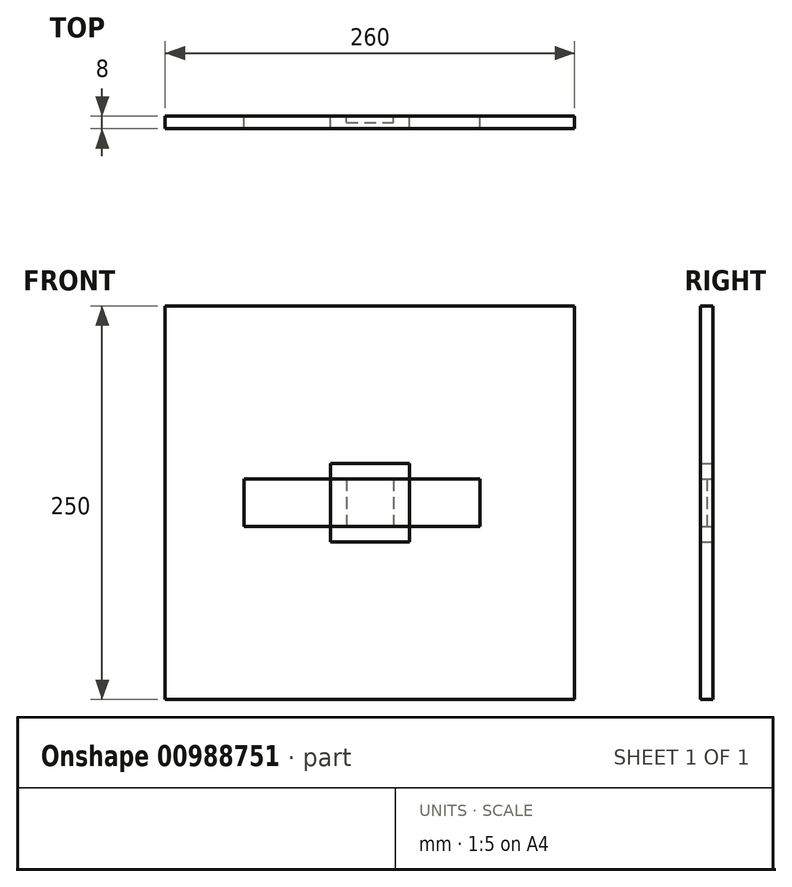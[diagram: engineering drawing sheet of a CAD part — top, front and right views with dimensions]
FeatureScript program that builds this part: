
annotation { "Feature Type Name" : "Feature", "Feature Type Description" : "" }
export const myFeature = defineFeature(function(context is Context, id is Id, definition is map)
    precondition{}
    {
        {
            var Q0;
            Q0=qCreatedBy(makeId("Front.planeOp"),FACE);
            var sketch = newSketch(context, id + "F0", { "sketchPlane" : qUnion([Q0])});
            skLineSegment(sketch, "E0.bottom", {"start": v(-130, 125) * mm, "end": v(130, 125) * mm});
            skLineSegment(sketch, "E0.top", {"start": v(-130, -125) * mm, "end": v(130, -125) * mm});
            skLineSegment(sketch, "E0.left", {"start": v(-130, 125) * mm, "end": v(-130, -125) * mm});
            skLineSegment(sketch, "E0.right", {"start": v(130, 125) * mm, "end": v(130, -125) * mm});
            skSolve(sketch);
        }
        {
            var Q0;
            Q0=makeQuery(id+"F0.imprint","IMPRINT",FACE,{"disambiguationData":[TD([[makeQuery(id+"F0.imprint","IMPRINT",EDGE,{"derivedFrom":sQuery(id+"F0.wireOp",EDGE,"E0.bottom")}),-1.0]])]});
            extrude(context, id + "F1", {"entities" : qUnion([Q0]), "depth" : 8 * mm, "offsetDistance" : 25 * mm});
        }
        {
            var Q0;
            Q0=qCreatedBy(makeId("Front.planeOp"),FACE);
            var sketch = newSketch(context, id + "F2", { "sketchPlane" : qUnion([Q0])});
            skLineSegment(sketch, "E1.bottom", {"start": v(-15, 15) * mm, "end": v(15, 15) * mm});
            skLineSegment(sketch, "E1.top", {"start": v(-15, -15) * mm, "end": v(15, -15) * mm});
            skLineSegment(sketch, "E1.left", {"start": v(-15, 15) * mm, "end": v(-15, -15) * mm});
            skLineSegment(sketch, "E1.right", {"start": v(15, 15) * mm, "end": v(15, -15) * mm});
            skSolve(sketch);
        }
        {
            var Q0;
            Q0=makeQuery(id+"F2.imprint","IMPRINT",FACE,{"disambiguationData":[TD([[makeQuery(id+"F2.imprint","IMPRINT",EDGE,{"derivedFrom":sQuery(id+"F2.wireOp",EDGE,"E1.bottom")}),-1.0]])]});
            extrude(context, id + "F3", {"entities" : qUnion([Q0]), "depth" : 4 * mm, "offsetDistance" : 25 * mm});
        }
        {
            var Q0;
            Q0=qCreatedBy(makeId("Front.planeOp"),FACE);
            var sketch = newSketch(context, id + "F4", { "sketchPlane" : qUnion([Q0])});
            skLineSegment(sketch, "E2.bottom", {"start": v(-25, 25) * mm, "end": v(25, 25) * mm});
            skLineSegment(sketch, "E2.top", {"start": v(-25, -25) * mm, "end": v(25, -25) * mm});
            skLineSegment(sketch, "E2.left", {"start": v(-25, 25) * mm, "end": v(-25, -25) * mm});
            skLineSegment(sketch, "E2.right", {"start": v(25, 25) * mm, "end": v(25, -25) * mm});
            skSolve(sketch);
        }
        {
            var Q0;
            Q0=makeQuery(id+"F4.imprint","IMPRINT",FACE,{"disambiguationData":[TD([[makeQuery(id+"F4.imprint","IMPRINT",EDGE,{"derivedFrom":sQuery(id+"F4.wireOp",EDGE,"E2.bottom")}),-1.0]])]});
            extrude(context, id + "F5", {"entities" : qUnion([Q0]), "depth" : 8 * mm, "offsetDistance" : 25 * mm});
        }
        {
            var Q0;
            Q0=qCreatedBy(makeId("Front.planeOp"),FACE);
            var sketch = newSketch(context, id + "F6", { "sketchPlane" : qUnion([Q0])});
            skLineSegment(sketch, "E3.bottom", {"start": v(-80, 15) * mm, "end": v(70, 15) * mm});
            skLineSegment(sketch, "E3.top", {"start": v(-80, -15) * mm, "end": v(70, -15) * mm});
            skLineSegment(sketch, "E3.left", {"start": v(-80, 15) * mm, "end": v(-80, -15) * mm});
            skLineSegment(sketch, "E3.right", {"start": v(70, 15) * mm, "end": v(70, -15) * mm});
            skSolve(sketch);
        }
        {
            var Q0;
            Q0=makeQuery(id+"F6.imprint","IMPRINT",FACE,{"disambiguationData":[TD([[makeQuery(id+"F6.imprint","IMPRINT",EDGE,{"derivedFrom":sQuery(id+"F6.wireOp",EDGE,"E3.bottom")}),-1.0]])]});
            extrude(context, id + "F7", {"entities" : qUnion([Q0]), "depth" : 8 * mm, "offsetDistance" : 25 * mm});
        }
    });
